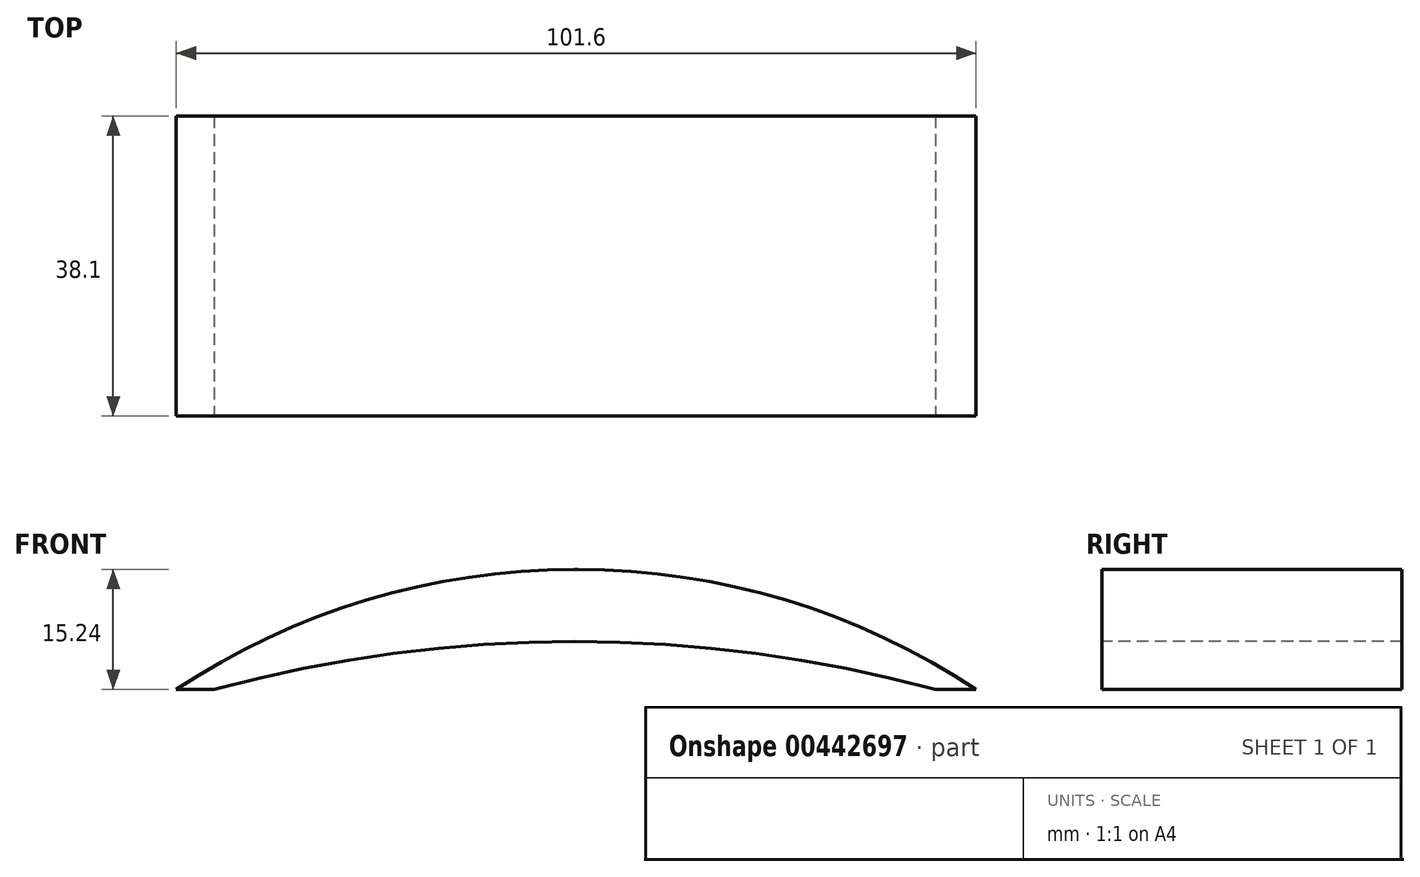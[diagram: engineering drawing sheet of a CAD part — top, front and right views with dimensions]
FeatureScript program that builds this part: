
annotation { "Feature Type Name" : "Feature", "Feature Type Description" : "" }
export const myFeature = defineFeature(function(context is Context, id is Id, definition is map)
    precondition{}
    {
        {
            var Q0;
            Q0=qCreatedBy(makeId("Top.planeOp"),FACE);
            var sketch = newSketch(context, id + "F0", { "sketchPlane" : qUnion([Q0])});
            skLineSegment(sketch, "E0.bottom", {"start": v(-14.7, 30.28) * mm, "end": v(36.1, 30.28) * mm});
            skLineSegment(sketch, "E0.top", {"start": v(-14.7, 11.23) * mm, "end": v(36.1, 11.23) * mm});
            skLineSegment(sketch, "E0.left", {"start": v(-14.7, 30.28) * mm, "end": v(-14.7, 11.23) * mm});
            skLineSegment(sketch, "E0.right", {"start": v(36.1, 30.28) * mm, "end": v(36.1, 11.23) * mm});
            skSolve(sketch);
        }
        {
            var Q0;
            Q0=makeQuery(id+"F0.imprint","IMPRINT",FACE,{"disambiguationData":[TD([[makeQuery(id+"F0.imprint","IMPRINT",EDGE,{"derivedFrom":sQuery(id+"F0.wireOp",EDGE,"E0.bottom")}),-1.0]])]});
            extrude(context, id + "F1", {"entities" : qUnion([Q0]), "depth" : 7.62 * mm});
        }
        {
            var Q0;
            Q0=makeQuery(id+"F1.opExtrude","SWEPT_FACE",FACE,{"disambiguationData":[OSD([sQuery(id+"F0.wireOp",EDGE,"E0.top")])]});
            var sketch = newSketch(context, id + "F2", { "sketchPlane" : qUnion([Q0])});
            skArc(sketch, "E1", {"start": v(33.52, 0) * mm, "mid": v(10.61, 3.04) * mm, "end": v(-12.3, 0) * mm});
            skSolve(sketch);
        }
        {
            var Q0;
            {var subQ0=sQuery(id+"F2.wireOp",EDGE,"E1");Q0=makeQuery(id+"F2.imprint","IMPRINT",FACE,{"disambiguationData":[TD([[makeQuery(id+"F2.imprint","IMPRINT",EDGE,{"derivedFrom":subQ0}),1.0]])]});}
            extrude(context, id + "F3", {"entities" : qUnion([Q0]), "operationType" : NewBodyOperationType.REMOVE, "oppositeDirection" : true, "depth" : 25.4 * mm});
        }
        {
            var Q0;
            Q0=makeQuery(id+"F1.opExtrude","CAP_EDGE",EDGE,{"disambiguationData":[OSD([sQuery(id+"F0.wireOp",EDGE,"E0.left")])],"isStart":false});
            var Q1;
            Q1=makeQuery(id+"F1.opExtrude","CAP_EDGE",EDGE,{"disambiguationData":[OSD([sQuery(id+"F0.wireOp",EDGE,"E0.right")])],"isStart":false});
            fillet(context, id + "F4", {"entities" : qUnion([Q0, Q1]), "radius" : 45.72 * mm, "tangentPropagation" : true, "allowEdgeOverflow" : false});
        }
        {
            var Q0;
            Q0=qCreatedBy(makeId("Top.planeOp"),FACE);
            cPlane(context, id + "F5", {"entities" : qUnion([Q0]), "cplaneType" : CPlaneType.OFFSET, "offset" : 7.62 * mm, "width" : 152.4 * mm, "height" : 152.4 * mm});
        }
        {
            var Q0;
            Q0=makeQuery(id+"F1.opExtrude","SWEPT_BODY",BODY,{"disambiguationData":[OSD([sQuery(id+"F0.wireOp",EDGE,"E0.bottom"),sQuery(id+"F0.wireOp",EDGE,"E0.top"),sQuery(id+"F0.wireOp",EDGE,"E0.left"),sQuery(id+"F0.wireOp",EDGE,"E0.right")])]});
            var Q1;
            {var subQ0=sQuery(id+"F0.wireOp",EDGE,"E0.bottom");var subQ1=makeQuery(id+"F1.opExtrude","SWEPT_FACE",FACE,{"disambiguationData":[OSD([subQ0])]});var subQ2=sQuery(id+"F0.wireOp",EDGE,"E0.top");var subQ3=sQuery(id+"F0.wireOp",EDGE,"E0.left");Q1=makeQuery(id+"F4.opFillet","BLEND_VERTEX",VERTEX,{"blendedFrom":[makeQuery(id+"F1.opExtrude","CAP_EDGE",EDGE,{"disambiguationData":[OSD([subQ3])],"isStart":false}),subQ1,makeQuery(id+"F3.boolean.opBoolean","SPLIT",FACE,{"disambiguationData":[TD([makeQuery(id+"F1.opExtrude","SWEPT_FACE",FACE,{"disambiguationData":[OSD([subQ3])]})])],"derivedFrom":makeQuery(id+"F1.opExtrude","CAP_FACE",FACE,{"disambiguationData":[OSD([subQ0,subQ2,subQ3,sQuery(id+"F0.wireOp",EDGE,"E0.right")])],"isStart":true})})],"blendedInto":[subQ1,makeQuery(id+"F3.boolean.opBoolean","SPLIT",FACE,{"disambiguationData":[TD([makeQuery(id+"F1.opExtrude","SWEPT_FACE",FACE,{"disambiguationData":[OSD([subQ3])]})])],"derivedFrom":makeQuery(id+"F1.opExtrude","CAP_FACE",FACE,{"disambiguationData":[OSD([subQ0,subQ2,subQ3,sQuery(id+"F0.wireOp",EDGE,"E0.right")])],"isStart":true})})]});}
            transform(context, id + "F6", {"entities" : qUnion([Q0]), "transformType" : TransformType.SCALE_UNIFORMLY, "scale" : 2, "scalePoint" : qUnion([Q1]), "makeCopy" : false});
        }
    });
